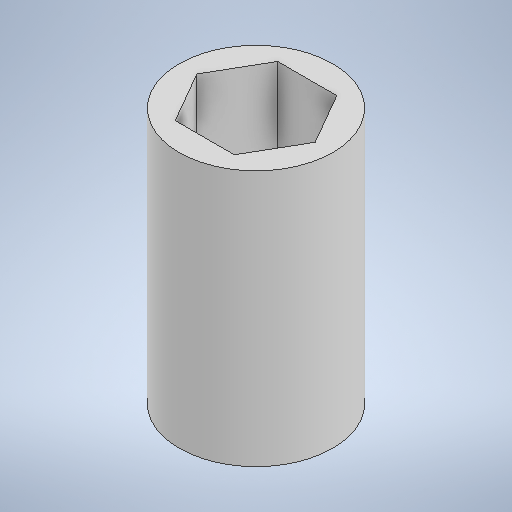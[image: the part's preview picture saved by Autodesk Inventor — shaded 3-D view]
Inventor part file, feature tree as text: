
AUTODESK INVENTOR PART (.ipt)
format: ipt  version: 2025 (Build 290162000, 162)  size: 210,944 bytes
history: native  units: mm
features: extrude x2, sketch x2
ambient origin geometry x8: Origin, YZ Plane, XZ Plane, XY Plane, X Axis, Y Axis, Z Axis, Center Point
bodies: Solid1 (feature_tree)
feature tree (4):
  extrude  "Extrusion1"  Depth=20.0mm TaperAngle=0.0deg
  extrude  "Extrusion2"  Depth=20.0mm TaperAngle=0.0deg
  sketch  "Sketch1"  dims[d0=12.0mm d1=20.0mm d2=0.0mm]
  sketch  "Sketch2"  dims[d3=8.0mm d4=20.0mm d5=0.0mm]
